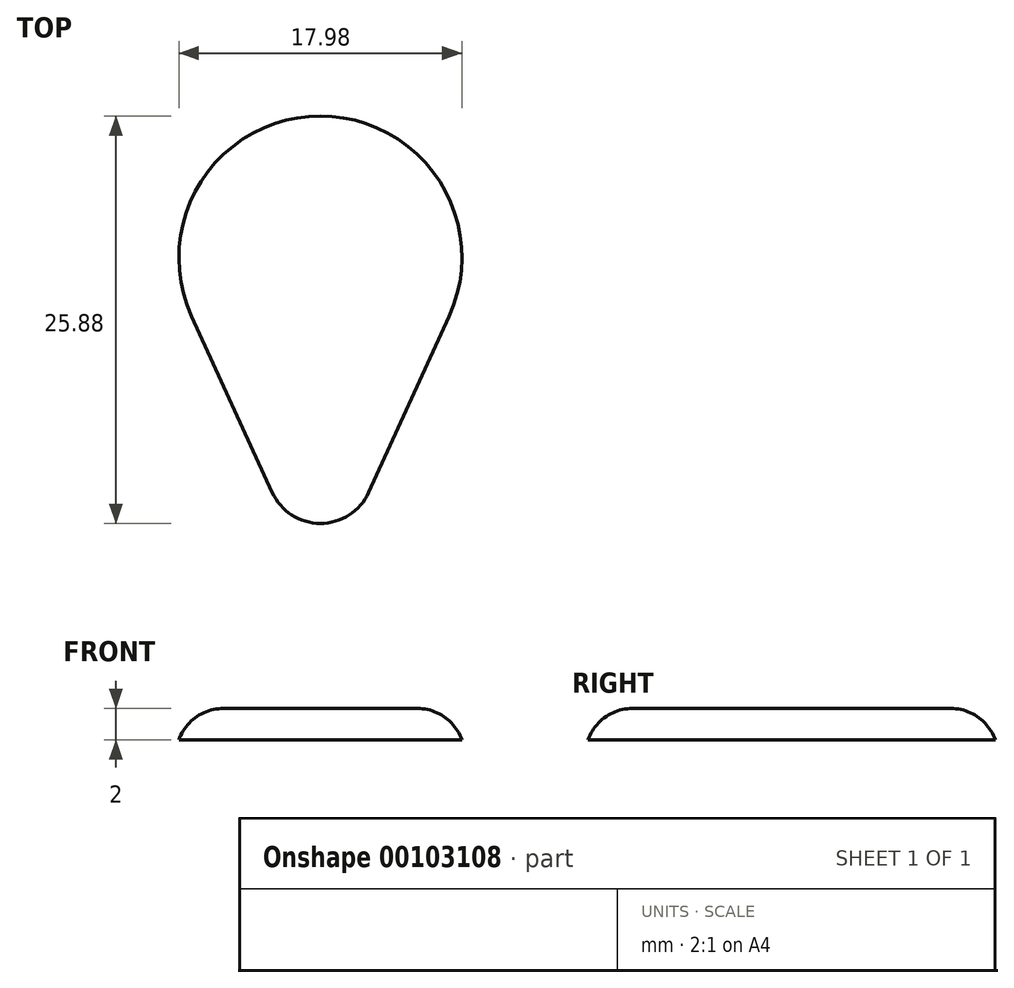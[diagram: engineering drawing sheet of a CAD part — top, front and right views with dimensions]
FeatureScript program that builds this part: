
annotation { "Feature Type Name" : "Feature", "Feature Type Description" : "" }
export const myFeature = defineFeature(function(context is Context, id is Id, definition is map)
    precondition{}
    {
        {
            var Q0;
            Q0=qCreatedBy(makeId("Top.planeOp"),FACE);
            var sketch = newSketch(context, id + "F0", { "sketchPlane" : qUnion([Q0])});
            skLineSegment(sketch, "E0", {"start": v(-3.07, -8.68) * mm, "end": v(-8.18, 2.5) * mm});
            skLineSegment(sketch, "E1.MirrorCS", {"start": v(3.07, -8.68) * mm, "end": v(8.18, 2.5) * mm});
            skArc(sketch, "E2", {"start": v(-3.07, -8.68) * mm, "mid": v(0, -10.65) * mm, "end": v(3.07, -8.68) * mm});
            skArc(sketch, "E3", {"start": v(8.18, 2.5) * mm, "mid": v(0, 15.23) * mm, "end": v(-8.18, 2.5) * mm});
            skSolve(sketch);
        }
        {
            var Q0;
            Q0=makeQuery(id+"F0.imprint","IMPRINT",FACE,{"disambiguationData":[TD([[makeQuery(id+"F0.imprint","IMPRINT",EDGE,{"derivedFrom":sQuery(id+"F0.wireOp",EDGE,"E0")}),-1.0]])]});
            extrude(context, id + "F1", {"entities" : qUnion([Q0]), "depth" : 2 * mm});
        }
        {
            var Q0;
            Q0=makeQuery(id+"F1.opExtrude","CAP_FACE",FACE,{"disambiguationData":[OSD([sQuery(id+"F0.wireOp",EDGE,"E0"),sQuery(id+"F0.wireOp",EDGE,"E1.MirrorCS"),sQuery(id+"F0.wireOp",EDGE,"E2"),sQuery(id+"F0.wireOp",EDGE,"E3")])],"isStart":false});
            fillet(context, id + "F2", {"entities" : qUnion([Q0]), "radius" : 3 * mm, "tangentPropagation" : true, "allowEdgeOverflow" : false});
        }
    });
